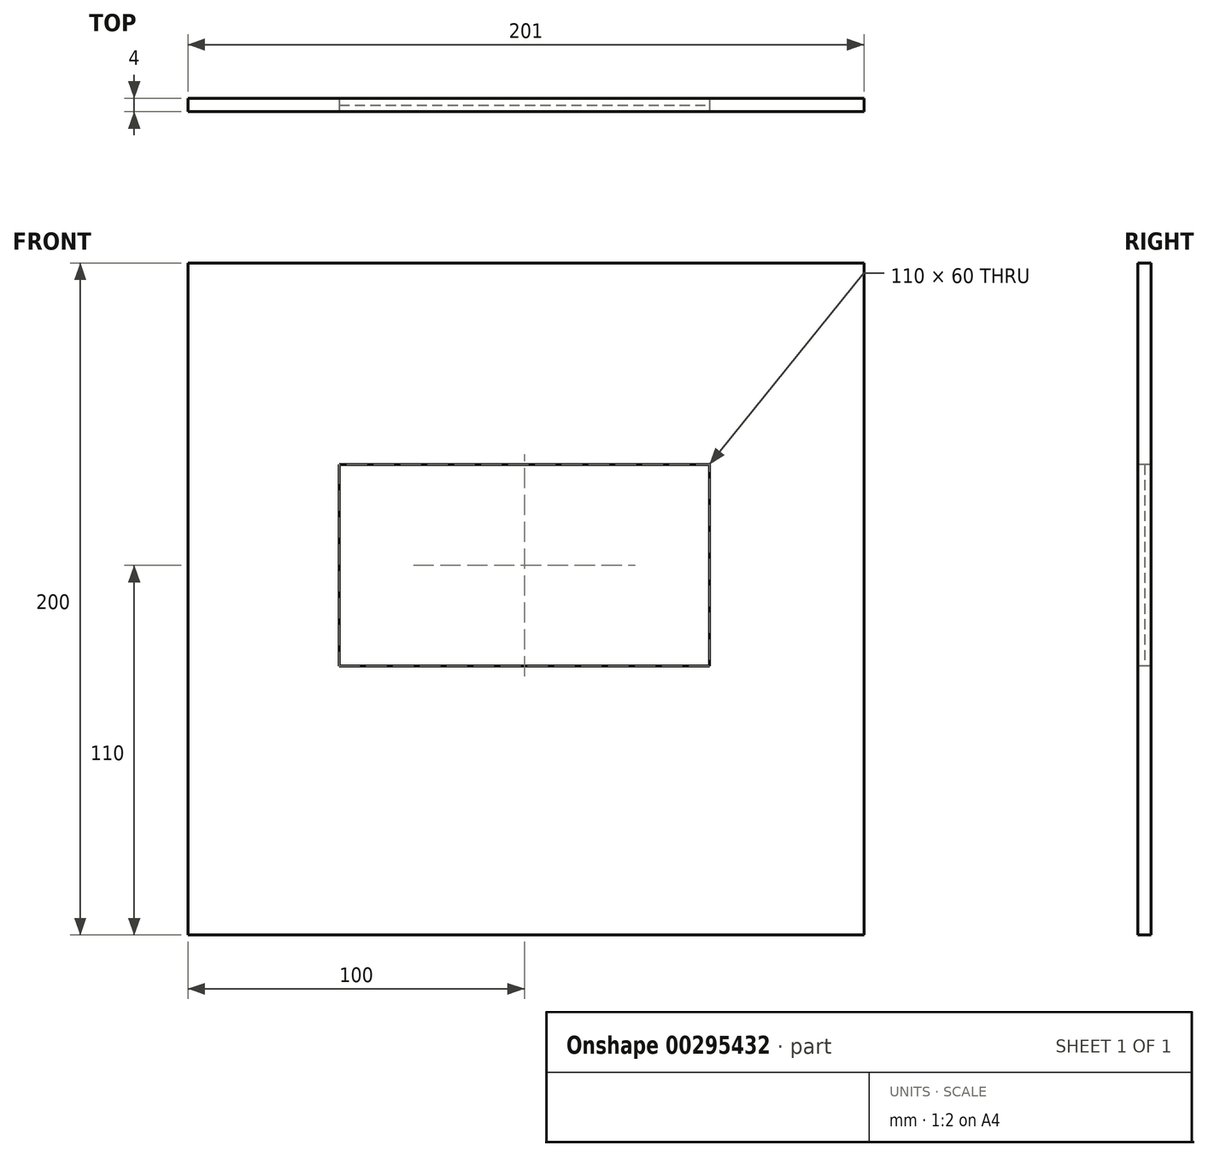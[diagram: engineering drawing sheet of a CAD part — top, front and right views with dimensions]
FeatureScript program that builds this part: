
annotation { "Feature Type Name" : "Feature", "Feature Type Description" : "" }
export const myFeature = defineFeature(function(context is Context, id is Id, definition is map)
    precondition{}
    {
        {
            var Q0;
            Q0=qCreatedBy(makeId("Front.planeOp"),FACE);
            var sketch = newSketch(context, id + "F0", { "sketchPlane" : qUnion([Q0])});
            skLineSegment(sketch, "E0.bottom", {"start": v(-75.5, 50) * mm, "end": v(125.5, 50) * mm});
            skLineSegment(sketch, "E0.top", {"start": v(-75.5, -150) * mm, "end": v(125.5, -150) * mm});
            skLineSegment(sketch, "E0.left", {"start": v(-75.5, 50) * mm, "end": v(-75.5, -150) * mm});
            skLineSegment(sketch, "E0.right", {"start": v(125.5, 50) * mm, "end": v(125.5, -150) * mm});
            skSolve(sketch);
        }
        {
            var Q0;
            Q0=makeQuery(id+"F0.imprint","IMPRINT",FACE,{"disambiguationData":[TD([[makeQuery(id+"F0.imprint","IMPRINT",EDGE,{"derivedFrom":sQuery(id+"F0.wireOp",EDGE,"E0.bottom")}),-1.0]])]});
            extrude(context, id + "F1", {"entities" : qUnion([Q0]), "depth" : 4 * mm});
        }
        {
            var Q0;
            Q0=makeQuery(id+"F1.opExtrude","CAP_FACE",FACE,{"disambiguationData":[OSD([sQuery(id+"F0.wireOp",EDGE,"E0.bottom"),sQuery(id+"F0.wireOp",EDGE,"E0.top"),sQuery(id+"F0.wireOp",EDGE,"E0.left"),sQuery(id+"F0.wireOp",EDGE,"E0.right")])],"isStart":false});
            var sketch = newSketch(context, id + "F2", { "sketchPlane" : qUnion([Q0])});
            skLineSegment(sketch, "E1", {"start": v(-75.5, -50) * mm, "end": v(-8.89, -50) * mm, "construction": true});
            skPoint(sketch, "E1.endSnap0", {"position": v(125.5, -50) * mm});
            skLineSegment(sketch, "E2.bottom", {"start": v(-30.5, -10) * mm, "end": v(79.5, -10) * mm});
            skLineSegment(sketch, "E2.top", {"start": v(-30.5, -70) * mm, "end": v(79.5, -70) * mm});
            skLineSegment(sketch, "E2.left", {"start": v(-30.5, -10) * mm, "end": v(-30.5, -70) * mm});
            skLineSegment(sketch, "E2.right", {"start": v(79.5, -10) * mm, "end": v(79.5, -70) * mm});
            skSolve(sketch);
        }
        {
            var Q0;
            Q0=makeQuery(id+"F2.imprint","IMPRINT",FACE,{"disambiguationData":[TD([[makeQuery(id+"F2.imprint","IMPRINT",EDGE,{"derivedFrom":sQuery(id+"F2.wireOp",EDGE,"E2.bottom")}),-1.0]])]});
            extrude(context, id + "F3", {"entities" : qUnion([Q0]), "operationType" : NewBodyOperationType.REMOVE, "oppositeDirection" : true, "depth" : 25 * mm});
        }
        {
            var Q0;
            Q0=makeQuery(id+"F1.opExtrude","CAP_FACE",FACE,{"disambiguationData":[OSD([sQuery(id+"F0.wireOp",EDGE,"E0.bottom"),sQuery(id+"F0.wireOp",EDGE,"E0.top"),sQuery(id+"F0.wireOp",EDGE,"E0.left"),sQuery(id+"F0.wireOp",EDGE,"E0.right")])],"isStart":false});
            var sketch = newSketch(context, id + "F4", { "sketchPlane" : qUnion([Q0])});
            skLineSegment(sketch, "E3.bottom", {"start": v(-30.5, -10) * mm, "end": v(79.5, -10) * mm});
            skLineSegment(sketch, "E3.top", {"start": v(-30.5, -70) * mm, "end": v(79.5, -70) * mm});
            skLineSegment(sketch, "E3.left", {"start": v(-30.5, -10) * mm, "end": v(-30.5, -70) * mm});
            skLineSegment(sketch, "E3.right", {"start": v(79.5, -10) * mm, "end": v(79.5, -70) * mm});
            skSolve(sketch);
        }
        {
            var Q0;
            Q0 = qSketchRegion(id + "F4", true);
            extrude(context, id + "F5", {"entities" : qUnion([Q0]), "oppositeDirection" : true, "depth" : 2 * mm});
        }
    });
